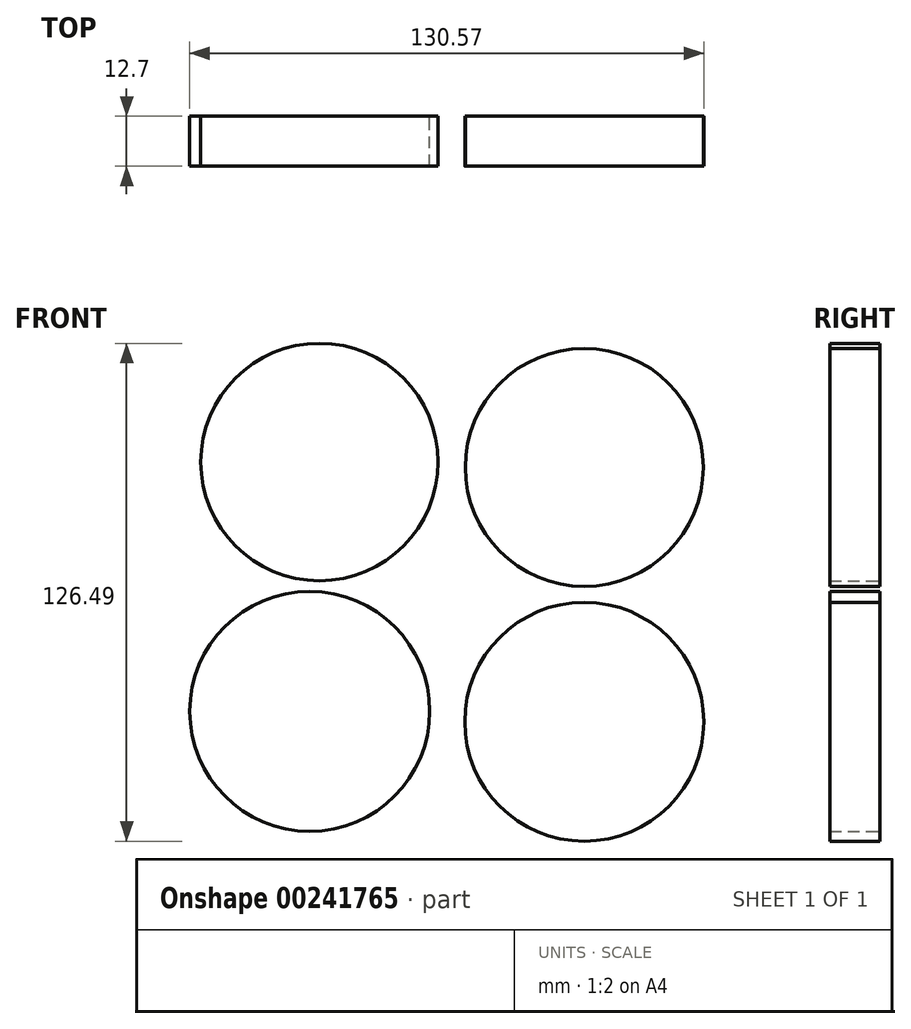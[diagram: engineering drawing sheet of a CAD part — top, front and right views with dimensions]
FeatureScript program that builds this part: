
annotation { "Feature Type Name" : "Feature", "Feature Type Description" : "" }
export const myFeature = defineFeature(function(context is Context, id is Id, definition is map)
    precondition{}
    {
        {
            var Q0;
            Q0=qCreatedBy(makeId("Front.planeOp"),FACE);
            var sketch = newSketch(context, id + "F0", { "sketchPlane" : qUnion([Q0])});
            skCircle(sketch, "E0", {"center": v(-67.28, 41.62) * mm, "radius": 30.15 * mm});
            skCircle(sketch, "E1", {"center": v(-69.74, -21.71) * mm, "radius": 30.48 * mm});
            skCircle(sketch, "E2", {"center": v(0, 40.26) * mm, "radius": 30.23 * mm});
            skCircle(sketch, "E3", {"center": v(0, -24.36) * mm, "radius": 30.35 * mm});
            skSolve(sketch);
        }
        {
            var Q0;
            Q0 = qSketchRegion(id + "F0", true);
            extrude(context, id + "F1", {"entities" : qUnion([Q0]), "depth" : 12.7 * mm});
        }
    });
